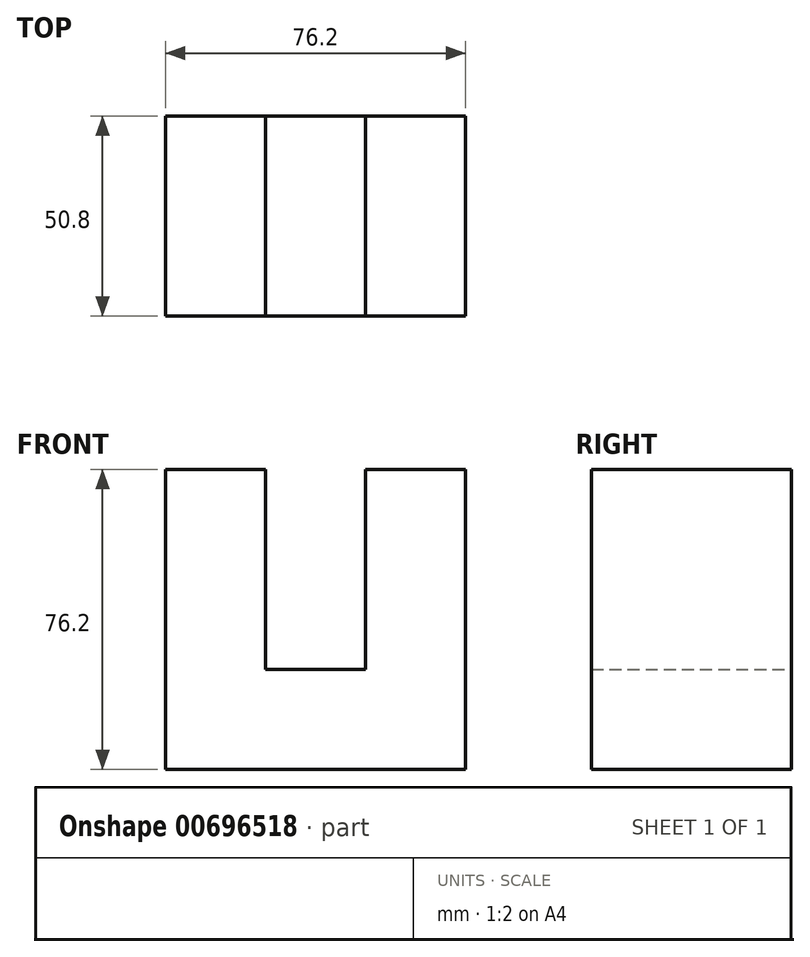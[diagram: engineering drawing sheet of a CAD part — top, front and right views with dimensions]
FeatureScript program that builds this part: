
annotation { "Feature Type Name" : "Feature", "Feature Type Description" : "" }
export const myFeature = defineFeature(function(context is Context, id is Id, definition is map)
    precondition{}
    {
        {
            var Q0;
            Q0=qCreatedBy(makeId("Front.planeOp"),FACE);
            var sketch = newSketch(context, id + "F0", { "sketchPlane" : qUnion([Q0])});
            skLineSegment(sketch, "E0", {"start": v(0, 0) * mm, "end": v(-25.4, 0) * mm});
            skLineSegment(sketch, "E1", {"start": v(-25.4, 0) * mm, "end": v(-25.4, -76.2) * mm});
            skLineSegment(sketch, "E2", {"start": v(-25.4, -76.2) * mm, "end": v(50.8, -76.2) * mm});
            skLineSegment(sketch, "E3", {"start": v(50.8, -76.2) * mm, "end": v(50.8, 0) * mm});
            skLineSegment(sketch, "E4", {"start": v(50.8, 0) * mm, "end": v(25.4, 0) * mm});
            skLineSegment(sketch, "E5", {"start": v(25.4, 0) * mm, "end": v(25.4, -50.8) * mm});
            skLineSegment(sketch, "E6", {"start": v(25.4, -50.8) * mm, "end": v(0, -50.8) * mm});
            skLineSegment(sketch, "E7", {"start": v(0, -50.8) * mm, "end": v(0, 0) * mm});
            skSolve(sketch);
        }
        {
            var Q0;
            Q0 = qSketchRegion(id + "F0", true);
            extrude(context, id + "F1", {"entities" : qUnion([Q0]), "depth" : 50.8 * mm, "offsetDistance" : 25.4 * mm});
        }
    });
